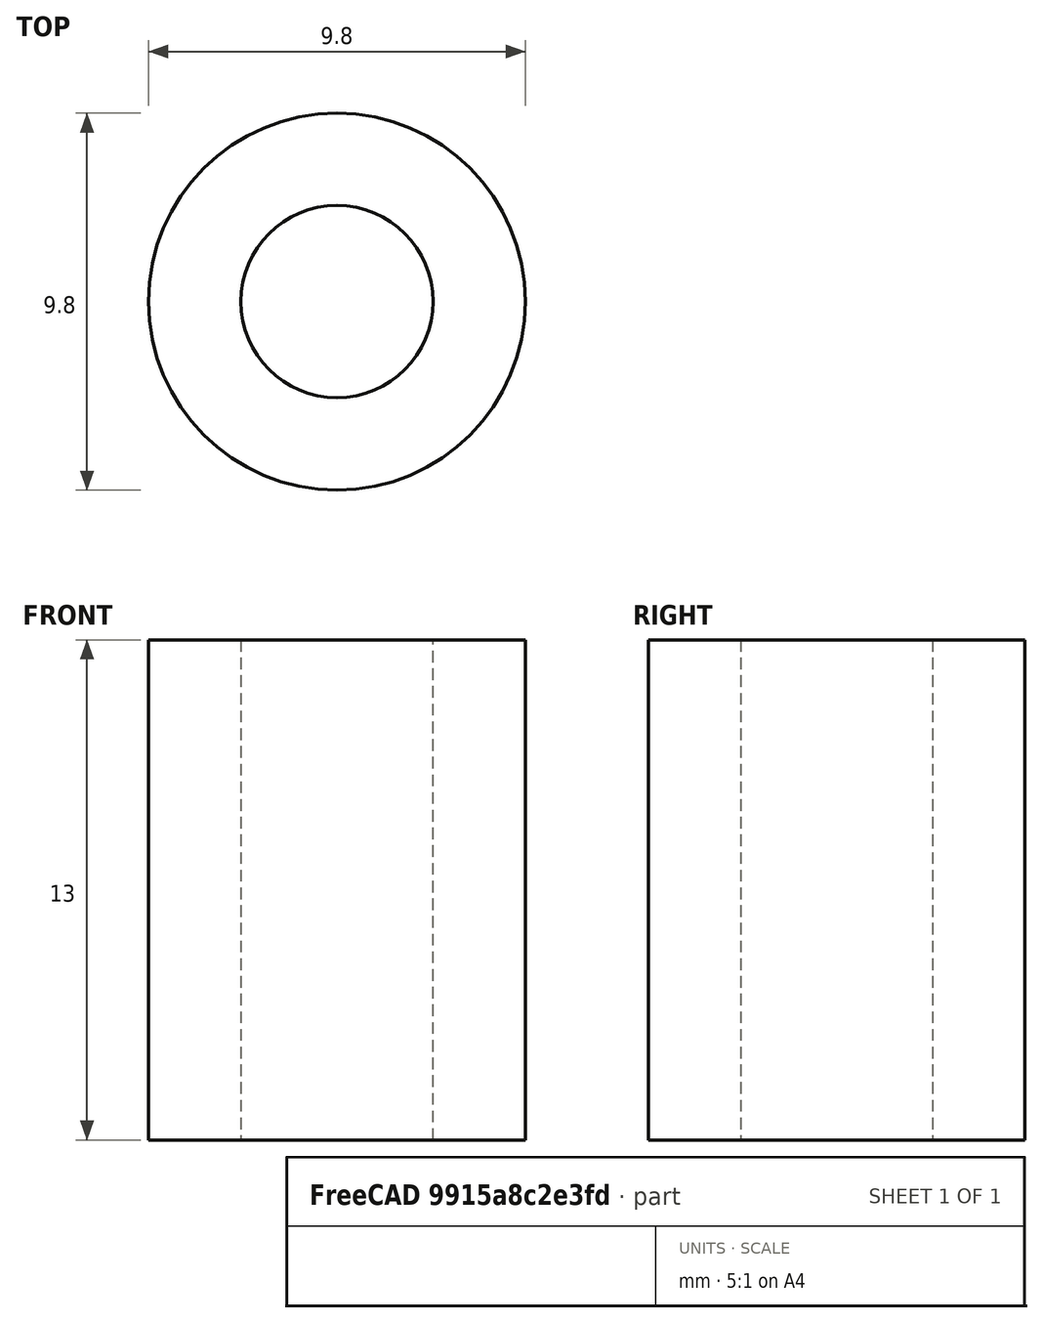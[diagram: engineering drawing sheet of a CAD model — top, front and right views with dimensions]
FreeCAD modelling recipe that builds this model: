
FCSTD DOCUMENT  (FreeCAD 2024.2R37179 (Git))
Label: spacer
License: All rights reserved
LicenseURL: https://en.wikipedia.org/wiki/All_rights_reserved
objects: Sketcher::SketchObject×1, PartDesign::Pad×1, PartDesign::Body×1
note: 4 computed .brp shape members not serialized (recipe doc carries the construction recipe); baked Part::Feature solids carry a one-line shape summary decoded from their .brp

FEATURE [Sketcher::SketchObject] Sketch
  AttachmentSupport = -> [XY_Plane]
  FullyConstrained = true
  MapMode = 5
  sketch-geometry (2):
    g0: Circle CenterX=0 CenterY=0 CenterZ=0 NormalX=0 NormalY=0 NormalZ=1 AngleXU=0 Radius=2.5
    g1: Circle CenterX=0 CenterY=0 CenterZ=0 NormalX=0 NormalY=0 NormalZ=1 AngleXU=0 Radius=4.9
  constraints (4):
    c: Coincident(g0,g-1)
    c: Coincident(g1,g0)
    c: Diameter(g1) = 9.8
    c: Diameter(g0) = 5
FEATURE [PartDesign::Pad] Pad
  Direction = (0,0,1)
  Length = 13
  Length2 = 10
  Profile = -> Sketch
  ReferenceAxis = -> Sketch [N_Axis]
  Refine = true
  Suppressed = false
  Type = 0
FEATURE [PartDesign::Body] Body
  Group = -> [Sketch,Pad]
  Origin = -> Origin
  Tip = -> Pad
